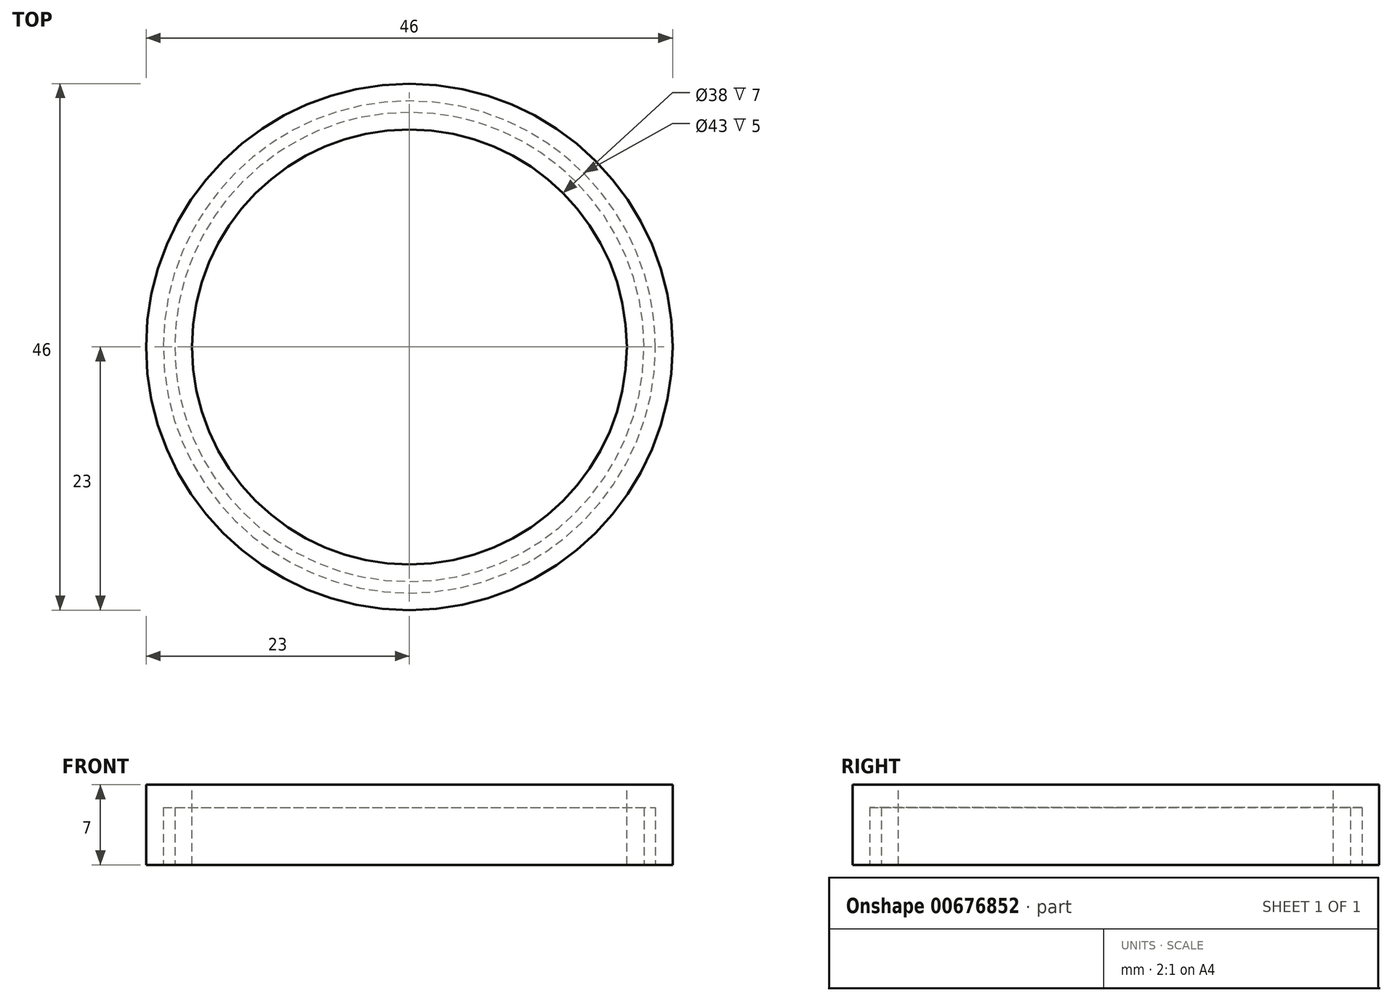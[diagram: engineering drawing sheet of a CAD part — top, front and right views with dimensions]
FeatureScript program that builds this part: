
annotation { "Feature Type Name" : "Feature", "Feature Type Description" : "" }
export const myFeature = defineFeature(function(context is Context, id is Id, definition is map)
    precondition{}
    {
        {
            var Q0;
            Q0=qCreatedBy(makeId("Top.planeOp"),FACE);
            var sketch = newSketch(context, id + "F0", { "sketchPlane" : qUnion([Q0])});
            skCircle(sketch, "E0", {"center": v(0, 0) * mm, "radius": 19 * mm});
            skCircle(sketch, "E1", {"center": v(0, 0) * mm, "radius": 23 * mm});
            skSolve(sketch);
        }
        {
            var Q0;
            Q0=makeQuery(id+"F0.imprint","IMPRINT",FACE,{"disambiguationData":[TD([[makeQuery(id+"F0.imprint","IMPRINT",EDGE,{"derivedFrom":sQuery(id+"F0.wireOp",EDGE,"E0")}),-1.0]])]});
            extrude(context, id + "F1", {"entities" : qUnion([Q0]), "oppositeDirection" : true, "depth" : 7 * mm, "offsetDistance" : 25 * mm});
        }
        {
            var Q0;
            Q0=makeQuery(id+"F1.opExtrude","CAP_FACE",FACE,{"disambiguationData":[OSD([sQuery(id+"F0.wireOp",EDGE,"E0"),sQuery(id+"F0.wireOp",EDGE,"E1")])],"isStart":false});
            var sketch = newSketch(context, id + "F2", { "sketchPlane" : qUnion([Q0])});
            skCircle(sketch, "E2", {"center": v(0, 0) * mm, "radius": 20.5 * mm});
            skCircle(sketch, "E3", {"center": v(0, 0) * mm, "radius": 21.5 * mm});
            skSolve(sketch);
        }
        {
            var Q0;
            Q0=makeQuery(id+"F2.imprint","IMPRINT",FACE,{"disambiguationData":[TD([[makeQuery(id+"F2.imprint","IMPRINT",EDGE,{"derivedFrom":sQuery(id+"F2.wireOp",EDGE,"E2")}),-1.0]])]});
            extrude(context, id + "F3", {"entities" : qUnion([Q0]), "operationType" : NewBodyOperationType.REMOVE, "oppositeDirection" : true, "depth" : 5 * mm, "offsetDistance" : 25 * mm});
        }
    });
